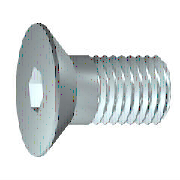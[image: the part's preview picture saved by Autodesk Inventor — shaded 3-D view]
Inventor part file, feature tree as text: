
AUTODESK INVENTOR PART (.ipt)
format: ipt  version: 2020 (Build 240168000, 168)  size: 189,440 bytes
history: native  units: mm (DEFAULTED — no unit token found)
features: other x5, sketch x2
ambient origin geometry x8: Origin, YZ Plane, XZ Plane, XY Plane, X Axis, Y Axis, Z Axis, Center Point
bodies: Solid1 (feature_tree)
feature tree (7):
  other  "WorkPoint1"
  sketch  "Skizze2"  dims[d0=45.0deg]
  other  "Drehung1"
  other  "MSC_A1"
  other  "MSC_PF1"
  other  "MSC_PT1"
  sketch  "Skizze3"  dims[d2=3.0mm d3=3.0mm d4=1.5mm d5=1.5mm d6=8.0mm d7=10.0mm d8=360.0deg d9=0.0mm d10=2.0mm d11=2.0mm d12=120.0deg d13=120.0deg d14=120.0deg d15=120.0deg d16=1.2mm d17=0.0mm d18=0.1mm d19=0.25mm d20=45.0deg d22=0.0mm d23=0.0mm d35=0.0mm d37=0.0mm d38=0.0mm d39=0.25mm d40=0.0mm d41=0.0mm d42=0.0mm d43=45.0deg]
